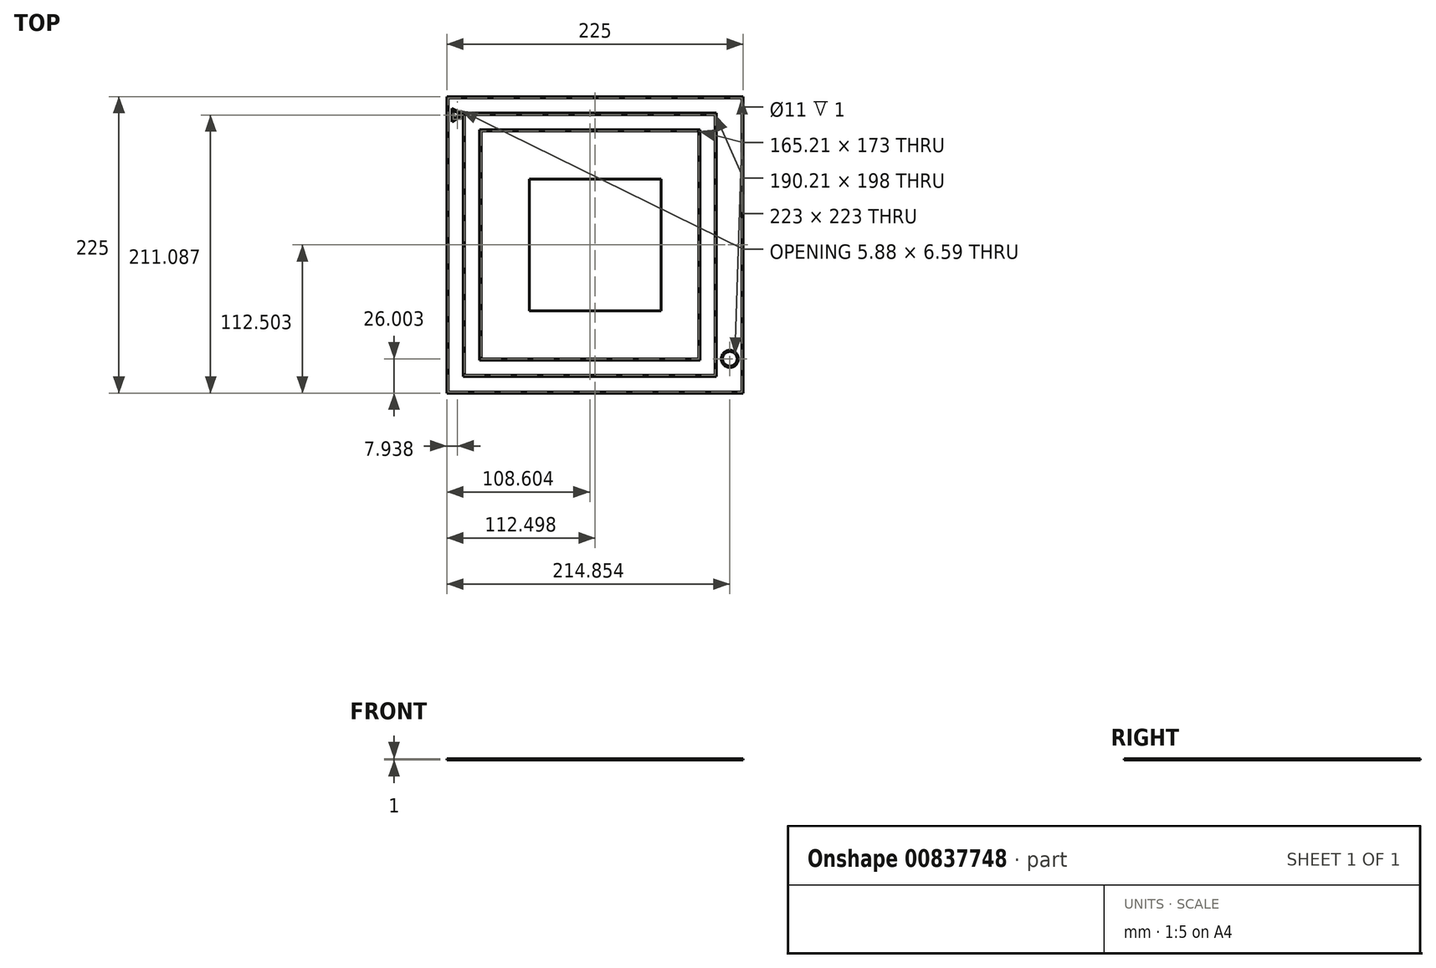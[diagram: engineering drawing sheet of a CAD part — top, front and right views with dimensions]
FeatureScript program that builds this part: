
annotation { "Feature Type Name" : "Feature", "Feature Type Description" : "" }
export const myFeature = defineFeature(function(context is Context, id is Id, definition is map)
    precondition{}
    {
        {
            assignVariable(context, id + "F0", {"name" : "LineHeight", "anyValue" : 1});
        }
        {
            var Q0;
            Q0=qCreatedBy(makeId("Top.planeOp"),FACE);
            var sketch = newSketch(context, id + "F1", { "sketchPlane" : qUnion([Q0])});
            skLineSegment(sketch, "E0.bottom", {"start": v(-91.48, 152.86) * mm, "end": v(133.52, 152.86) * mm});
            skLineSegment(sketch, "E0.top", {"start": v(-91.48, -72.14) * mm, "end": v(133.52, -72.14) * mm});
            skLineSegment(sketch, "E0.left", {"start": v(-91.48, 152.86) * mm, "end": v(-91.48, -72.14) * mm});
            skLineSegment(sketch, "E0.right", {"start": v(133.52, 152.86) * mm, "end": v(133.52, -72.14) * mm});
            skLineSegment(sketch, "E1.bottom", {"start": v(-78.98, 140.36) * mm, "end": v(113.23, 140.36) * mm});
            skLineSegment(sketch, "E1.top", {"start": v(-78.98, -59.64) * mm, "end": v(113.23, -59.64) * mm});
            skLineSegment(sketch, "E1.left", {"start": v(-78.98, 140.36) * mm, "end": v(-78.98, -59.64) * mm});
            skLineSegment(sketch, "E1.right", {"start": v(113.23, 140.36) * mm, "end": v(113.23, -59.64) * mm});
            skLineSegment(sketch, "E2.bottom", {"start": v(-66.48, 127.86) * mm, "end": v(100.73, 127.86) * mm});
            skLineSegment(sketch, "E2.top", {"start": v(-66.48, -47.14) * mm, "end": v(100.73, -47.14) * mm});
            skLineSegment(sketch, "E2.left", {"start": v(-66.48, 127.86) * mm, "end": v(-66.48, -47.14) * mm});
            skLineSegment(sketch, "E2.right", {"start": v(100.73, 127.86) * mm, "end": v(100.73, -47.14) * mm});
            skLineSegment(sketch, "E3.bottom", {"start": v(-28.98, 90.36) * mm, "end": v(71.02, 90.36) * mm});
            skLineSegment(sketch, "E3.top", {"start": v(-28.98, -9.64) * mm, "end": v(71.02, -9.64) * mm});
            skLineSegment(sketch, "E3.left", {"start": v(-28.98, 90.36) * mm, "end": v(-28.98, -9.64) * mm});
            skLineSegment(sketch, "E3.right", {"start": v(71.02, 90.36) * mm, "end": v(71.02, -9.64) * mm});
            skLineSegment(sketch, "E4", {"start": v(-87.48, 143.86) * mm, "end": v(-87.48, 133.86) * mm});
            skLineSegment(sketch, "E5", {"start": v(-87.48, 133.86) * mm, "end": v(-78.55, 139.36) * mm});
            skLineSegment(sketch, "E6", {"start": v(-78.55, 139.36) * mm, "end": v(-87.48, 143.86) * mm});
            skCircle(sketch, "E7", {"center": v(123.37, -46.14) * mm, "radius": 6.5 * mm});
            skLineSegment(sketch, "E8", {"start": v(113.23, -46.14) * mm, "end": v(133.52, -46.14) * mm, "construction": true});
            skLineSegment(sketch, "E9", {"start": v(-90.48, 151.86) * mm, "end": v(132.52, 151.86) * mm});
            skLineSegment(sketch, "E10", {"start": v(132.52, 151.86) * mm, "end": v(132.52, -71.14) * mm});
            skLineSegment(sketch, "E11", {"start": v(132.52, -71.14) * mm, "end": v(-90.48, -71.14) * mm});
            skLineSegment(sketch, "E12", {"start": v(-90.48, -71.14) * mm, "end": v(-90.48, 151.86) * mm});
            skLineSegment(sketch, "E13", {"start": v(-77.98, 139.36) * mm, "end": v(112.23, 139.36) * mm});
            skLineSegment(sketch, "E14", {"start": v(112.23, 139.36) * mm, "end": v(112.23, -58.64) * mm});
            skLineSegment(sketch, "E15", {"start": v(112.23, -58.64) * mm, "end": v(-77.98, -58.64) * mm});
            skLineSegment(sketch, "E16", {"start": v(-77.98, -58.64) * mm, "end": v(-77.98, 139.36) * mm});
            skLineSegment(sketch, "E17", {"start": v(-65.48, 126.86) * mm, "end": v(99.73, 126.86) * mm});
            skLineSegment(sketch, "E18", {"start": v(99.73, 126.86) * mm, "end": v(99.73, -46.14) * mm});
            skLineSegment(sketch, "E19", {"start": v(99.73, -46.14) * mm, "end": v(-65.48, -46.14) * mm});
            skLineSegment(sketch, "E20", {"start": v(-65.48, -46.14) * mm, "end": v(-65.48, 126.86) * mm});
            skCircle(sketch, "E21", {"center": v(123.37, -46.14) * mm, "radius": 5.5 * mm});
            skLineSegment(sketch, "E22", {"start": v(-86.48, 142.24) * mm, "end": v(-80.6, 139.28) * mm});
            skPoint(sketch, "E22.startSnap0", {"position": v(-84.41, 142.24) * mm});
            skLineSegment(sketch, "E23", {"start": v(-80.6, 139.28) * mm, "end": v(-86.48, 135.65) * mm});
            skLineSegment(sketch, "E24", {"start": v(-86.48, 135.65) * mm, "end": v(-86.48, 142.24) * mm});
            skSolve(sketch);
        }
        {
            var Q0;
            Q0=makeQuery(id+"F1.imprint","IMPRINT",FACE,{"disambiguationData":[TD([[makeQuery(id+"F1.imprint","IMPRINT",EDGE,{"derivedFrom":sQuery(id+"F1.wireOp",EDGE,"E0.bottom")}),-1.0]])]});
            var Q1;
            Q1=makeQuery(id+"F1.imprint","IMPRINT",FACE,{"disambiguationData":[TD([[makeQuery(id+"F1.imprint","IMPRINT",EDGE,{"derivedFrom":sQuery(id+"F1.wireOp",EDGE,"E1.bottom")}),-1.0]])]});
            var Q2;
            Q2=makeQuery(id+"F1.imprint","IMPRINT",FACE,{"disambiguationData":[TD([[makeQuery(id+"F1.imprint","IMPRINT",EDGE,{"derivedFrom":sQuery(id+"F1.wireOp",EDGE,"E2.bottom")}),-1.0]])]});
            var Q3;
            Q3=makeQuery(id+"F1.imprint","IMPRINT",FACE,{"disambiguationData":[TD([[makeQuery(id+"F1.imprint","IMPRINT",EDGE,{"derivedFrom":sQuery(id+"F1.wireOp",EDGE,"E7")}),1.0]])]});
            var Q4;
            Q4=makeQuery(id+"F1.imprint","IMPRINT",FACE,{"disambiguationData":[TD([[makeQuery(id+"F1.imprint","IMPRINT",EDGE,{"derivedFrom":sQuery(id+"F1.wireOp",EDGE,"E3.bottom")}),-1.0]])]});
            var Q5;
            Q5=makeQuery(id+"F1.imprint","IMPRINT",FACE,{"disambiguationData":[TD([[makeQuery(id+"F1.imprint","IMPRINT",EDGE,{"derivedFrom":sQuery(id+"F1.wireOp",EDGE,"E4")}),1.0]])]});
            extrude(context, id + "F2", {"entities" : qUnion([Q0, Q1, Q2, Q3, Q4, Q5]), "depth" : (getVariable(context, 'LineHeight')) * mm, "offsetDistance" : 25 * mm});
        }
    });
